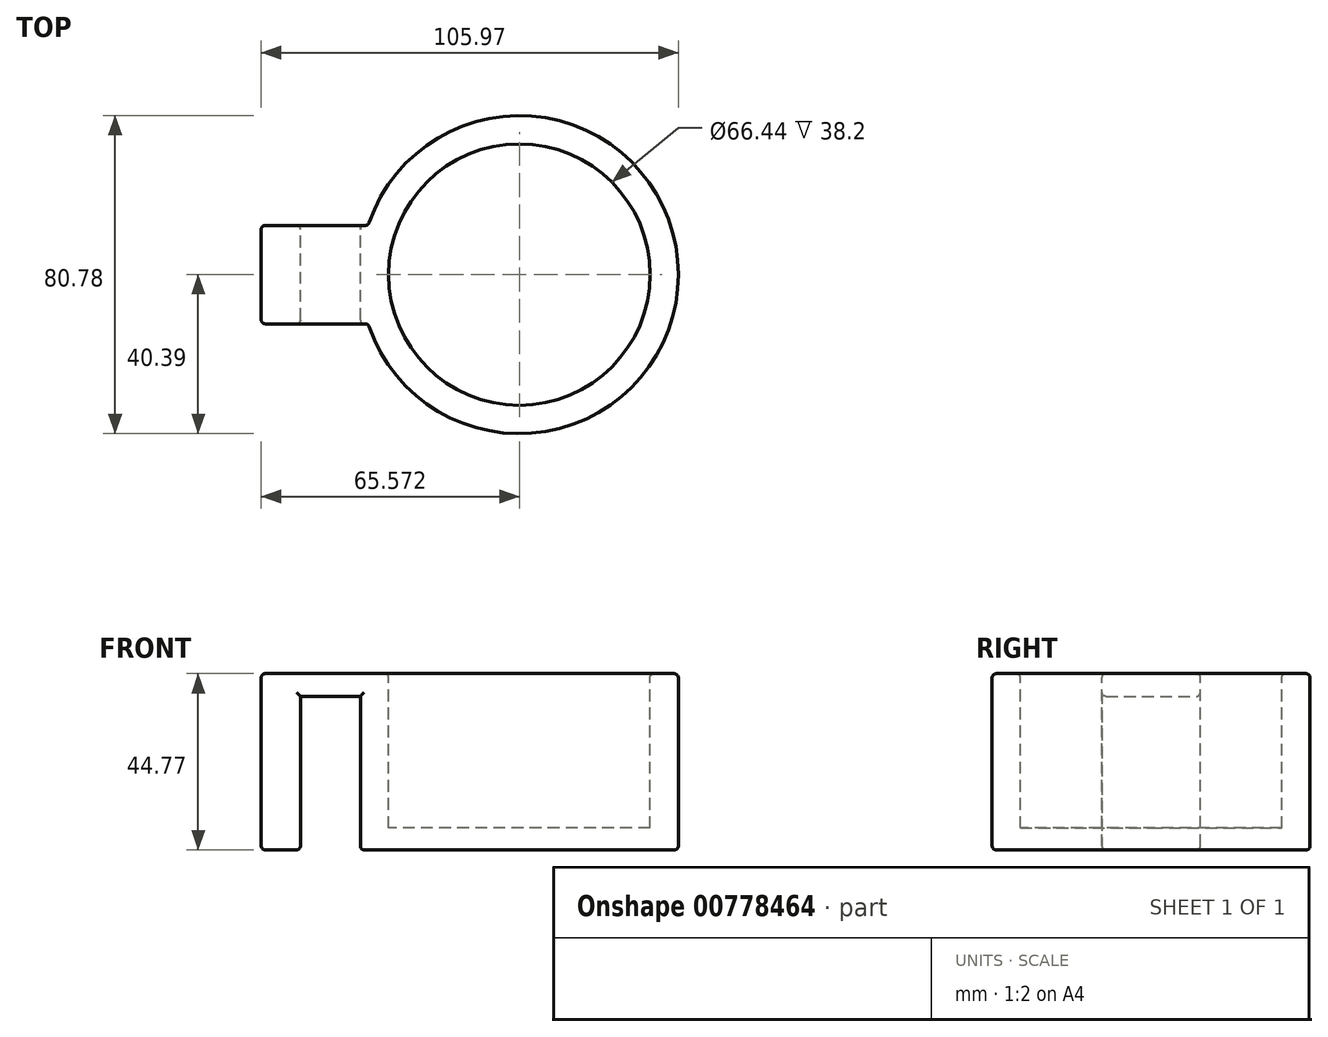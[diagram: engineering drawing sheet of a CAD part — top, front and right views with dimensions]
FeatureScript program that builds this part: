
annotation { "Feature Type Name" : "Feature", "Feature Type Description" : "" }
export const myFeature = defineFeature(function(context is Context, id is Id, definition is map)
    precondition{}
    {
        {
            var Q0;
            Q0=qCreatedBy(makeId("Front.planeOp"),FACE);
            var sketch = newSketch(context, id + "F0", { "sketchPlane" : qUnion([Q0])});
            skLineSegment(sketch, "E0", {"start": v(-32.35, 0) * mm, "end": v(-32.35, 44.77) * mm});
            skLineSegment(sketch, "E1", {"start": v(-32.35, 44.77) * mm, "end": v(-22.4, 44.77) * mm});
            skLineSegment(sketch, "E2", {"start": v(-22.4, 39.02) * mm, "end": v(-22.4, 0) * mm});
            skLineSegment(sketch, "E3", {"start": v(-22.4, 0) * mm, "end": v(-32.35, 0) * mm});
            skLineSegment(sketch, "E4", {"start": v(-22.4, 44.77) * mm, "end": v(-7.17, 44.77) * mm});
            skLineSegment(sketch, "E5", {"start": v(-7.17, 0) * mm, "end": v(-7.17, 39.02) * mm});
            skLineSegment(sketch, "E6", {"start": v(-22.4, 39.02) * mm, "end": v(-7.17, 39.02) * mm});
            skLineSegment(sketch, "E7", {"start": v(-7.17, 44.77) * mm, "end": v(33.22, 44.77) * mm});
            skLineSegment(sketch, "E8", {"start": v(33.22, 44.77) * mm, "end": v(33.22, 0) * mm});
            skLineSegment(sketch, "E9", {"start": v(33.22, 0) * mm, "end": v(-7.17, 0) * mm});
            skLineSegment(sketch, "E10", {"start": v(-22.4, 44.77) * mm, "end": v(-22.4, 39.02) * mm, "construction": true});
            skLineSegment(sketch, "E11", {"start": v(-7.17, 44.77) * mm, "end": v(-7.17, 39.02) * mm});
            skSolve(sketch);
        }
        {
            var Q0;
            Q0=makeQuery(id+"F0.imprint","IMPRINT",FACE,{"disambiguationData":[TD([[makeQuery(id+"F0.imprint","IMPRINT",EDGE,{"derivedFrom":sQuery(id+"F0.wireOp",EDGE,"E5")}),-1.0]])]});
            var Q1;
            Q1=sQuery(id+"F0.wireOp",EDGE,"E8");
            revolve(context, id + "F1", {"surfaceOperationType" : NewSurfaceOperationType.NEW, "entities" : qUnion([Q0]), "axis" : qUnion([Q1]), "revolveType" : RevolveType.FULL});
        }
        {
            var Q0;
            Q0=makeQuery(id+"F0.imprint","IMPRINT",FACE,{"disambiguationData":[TD([[makeQuery(id+"F0.imprint","IMPRINT",EDGE,{"derivedFrom":sQuery(id+"F0.wireOp",EDGE,"E0")}),-1.0]])]});
            var Q1;
            {var subQ2=sQuery(id+"F0.wireOp",EDGE,"E5");Q1=makeQuery(id+"F0.imprint","IMPRINT",FACE,{"disambiguationData":[TD([[makeQuery(id+"F0.imprint","IMPRINT",EDGE,{"derivedFrom":subQ2}),-1.0]])]});}
            extrude(context, id + "F2", {"entities" : qUnion([Q0, Q1]), "operationType" : NewBodyOperationType.ADD, "endBound" : BoundingType.SYMMETRIC, "depth" : 25 * mm, "offsetDistance" : 25 * mm});
        }
        {
            var Q0;
            {var subQ0=sQuery(id+"F0.wireOp",EDGE,"E7");Q0=makeQuery(id+"F2.boolean.opBoolean","MERGE",FACE,{"derivedFrom":[makeQuery(id+"F1.opRevolve","SWEPT_FACE",FACE,{"disambiguationData":[OSD([subQ0])]}),makeQuery(id+"F2.opExtrude","SWEPT_FACE",FACE,{"disambiguationData":[OSD([sQuery(id+"F0.wireOp",EDGE,"E1"),sQuery(id+"F0.wireOp",EDGE,"E4"),subQ0])]})]});}
            var sketch = newSketch(context, id + "F3", { "sketchPlane" : qUnion([Q0])});
            skCircle(sketch, "E12", {"center": v(33.22, 0) * mm, "radius": 33.22 * mm});
            skSolve(sketch);
        }
        {
            var Q0;
            Q0=makeQuery(id+"F3.imprint","IMPRINT",FACE,{"disambiguationData":[TD([[makeQuery(id+"F3.imprint","IMPRINT",EDGE,{"derivedFrom":sQuery(id+"F3.wireOp",EDGE,"E12")}),1.0]])]});
            extrude(context, id + "F4", {"entities" : qUnion([Q0]), "operationType" : NewBodyOperationType.REMOVE, "oppositeDirection" : true, "depth" : 39.2 * mm, "offsetDistance" : 25 * mm});
        }
        {
            var Q0;
            Q0=makeQuery(id+"F1.opRevolve","SWEPT_EDGE",EDGE,{"disambiguationData":[OSD([sQuery(id+"F0.wireOp",EDGE,"E4"),sQuery(id+"F0.wireOp",EDGE,"E7"),sQuery(id+"F0.wireOp",EDGE,"E11")])]});
            var Q1;
            Q1=makeQuery(id+"F4.boolean.opBoolean","COPY",EDGE,{"derivedFrom":makeQuery(id+"F4.opExtrude","CAP_EDGE",EDGE,{"disambiguationData":[OSD([sQuery(id+"F3.wireOp",EDGE,"E12")])],"isStart":true})});
            var Q2;
            {var subQ0=sQuery(id+"F0.wireOp",EDGE,"E7");Q2=makeQuery(id+"F2.boolean.opBoolean","MERGE",FACE,{"derivedFrom":[makeQuery(id+"F1.opRevolve","SWEPT_FACE",FACE,{"disambiguationData":[OSD([subQ0])]}),makeQuery(id+"F2.opExtrude","SWEPT_FACE",FACE,{"disambiguationData":[OSD([sQuery(id+"F0.wireOp",EDGE,"E1"),sQuery(id+"F0.wireOp",EDGE,"E4"),subQ0])]})]});}
            var Q3;
            Q3=makeQuery(id+"F2.opExtrude","CAP_FACE",FACE,{"disambiguationData":[OSD([sQuery(id+"F0.wireOp",EDGE,"E0"),sQuery(id+"F0.wireOp",EDGE,"E1"),sQuery(id+"F0.wireOp",EDGE,"E2"),sQuery(id+"F0.wireOp",EDGE,"E3"),sQuery(id+"F0.wireOp",EDGE,"E4"),sQuery(id+"F0.wireOp",EDGE,"E5"),sQuery(id+"F0.wireOp",EDGE,"E6"),sQuery(id+"F0.wireOp",EDGE,"E7"),sQuery(id+"F0.wireOp",EDGE,"E8"),sQuery(id+"F0.wireOp",EDGE,"E9")])],"isStart":false});
            var Q4;
            Q4=makeQuery(id+"F2.opExtrude","SWEPT_FACE",FACE,{"disambiguationData":[OSD([sQuery(id+"F0.wireOp",EDGE,"E0")])]});
            var Q5;
            Q5=makeQuery(id+"F2.opExtrude","CAP_FACE",FACE,{"disambiguationData":[OSD([sQuery(id+"F0.wireOp",EDGE,"E0"),sQuery(id+"F0.wireOp",EDGE,"E1"),sQuery(id+"F0.wireOp",EDGE,"E2"),sQuery(id+"F0.wireOp",EDGE,"E3"),sQuery(id+"F0.wireOp",EDGE,"E4"),sQuery(id+"F0.wireOp",EDGE,"E5"),sQuery(id+"F0.wireOp",EDGE,"E6"),sQuery(id+"F0.wireOp",EDGE,"E7"),sQuery(id+"F0.wireOp",EDGE,"E8"),sQuery(id+"F0.wireOp",EDGE,"E9")])],"isStart":true});
            var Q6;
            Q6=makeQuery(id+"F1.opRevolve","SWEPT_EDGE",EDGE,{"disambiguationData":[OSD([sQuery(id+"F0.wireOp",EDGE,"E5"),sQuery(id+"F0.wireOp",EDGE,"E9")])]});
            var Q7;
            {var subQ0=sQuery(id+"F0.wireOp",EDGE,"E9");Q7=makeQuery(id+"F2.boolean.opBoolean","MERGE",FACE,{"derivedFrom":[makeQuery(id+"F1.opRevolve","SWEPT_FACE",FACE,{"disambiguationData":[OSD([subQ0])]}),makeQuery(id+"F2.opExtrude","SWEPT_FACE",FACE,{"disambiguationData":[OSD([subQ0])]})]});}
            var Q8;
            Q8=makeQuery(id+"F2.opExtrude","SWEPT_FACE",FACE,{"disambiguationData":[OSD([sQuery(id+"F0.wireOp",EDGE,"E3")])]});
            fillet(context, id + "F5", {"entities" : qUnion([Q0, Q1, Q2, Q3, Q4, Q5, Q6, Q7, Q8]), "radius" : 1 * mm, "tangentPropagation" : true, "allowEdgeOverflow" : false});
        }
    });
